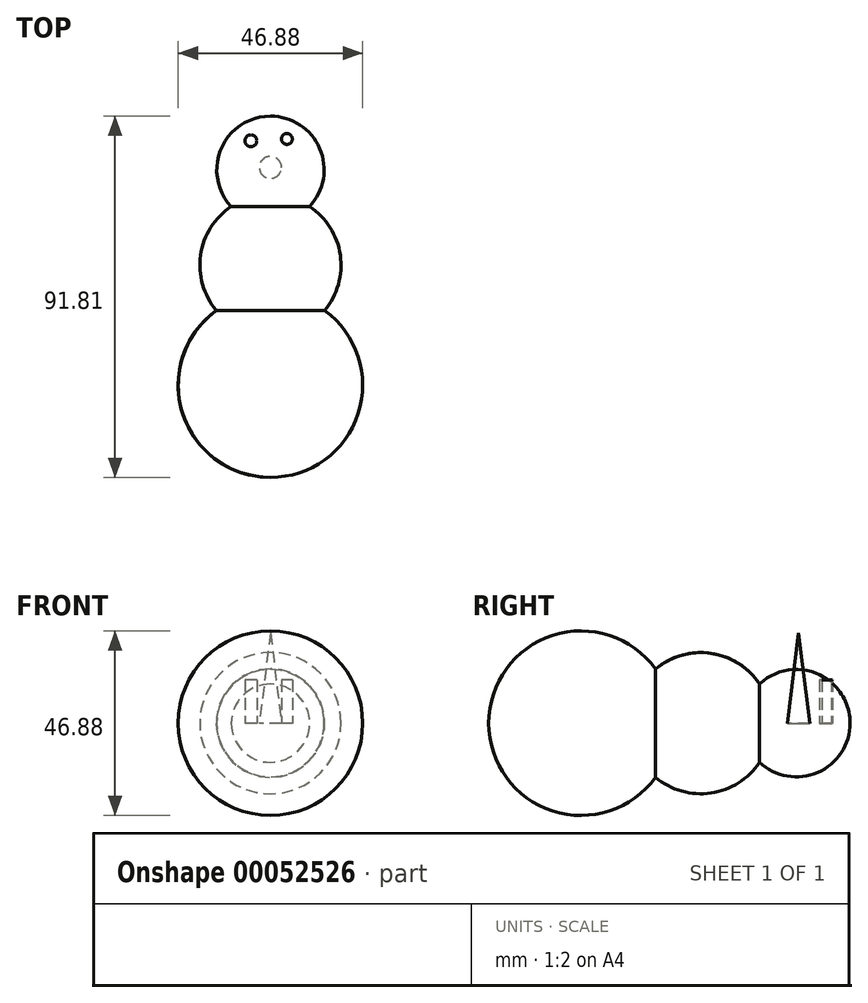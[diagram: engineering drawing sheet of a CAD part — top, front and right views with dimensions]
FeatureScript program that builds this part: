
annotation { "Feature Type Name" : "Feature", "Feature Type Description" : "" }
export const myFeature = defineFeature(function(context is Context, id is Id, definition is map)
    precondition{}
    {
        {
            var Q0;
            Q0=qCreatedBy(makeId("Top.planeOp"),FACE);
            var sketch = newSketch(context, id + "F0", { "sketchPlane" : qUnion([Q0])});
            skArc(sketch, "E0", {"start": v(0, 76.33) * mm, "mid": v(-12.52, 68.12) * mm, "end": v(-9.95, 53.36) * mm});
            skArc(sketch, "E1", {"start": v(-13.76, 26.95) * mm, "mid": v(-22.3, 0.73) * mm, "end": v(0, -15.48) * mm});
            skLineSegment(sketch, "E2", {"start": v(0, 76.33) * mm, "end": v(0, -15.48) * mm});
            skArc(sketch, "E3.trimOffspring", {"start": v(-9.95, 53.36) * mm, "mid": v(-17.75, 41) * mm, "end": v(-13.76, 26.95) * mm});
            skSolve(sketch);
        }
        {
            var Q0;
            Q0=qCreatedBy(makeId("Top.planeOp"),FACE);
            var sketch = newSketch(context, id + "F1", { "sketchPlane" : qUnion([Q0])});
            skCircle(sketch, "E4", {"center": v(0, 63.28) * mm, "radius": 2.82 * mm});
            skSolve(sketch);
        }
        {
            var Q0;
            Q0=makeQuery(id+"F1.imprint","IMPRINT",FACE,{"disambiguationData":[TD([[makeQuery(id+"F1.imprint","IMPRINT",EDGE,{"derivedFrom":sQuery(id+"F1.wireOp",EDGE,"E4")}),1.0]])]});
            extrude(context, id + "F2", {"entities" : qUnion([Q0]), "depth" : 76.2 * mm, "hasDraft" : true, "draftAngle" : 7 * degree, "draftPullDirection" : true});
        }
        {
            var Q0;
            Q0=makeQuery(id+"F0.imprint","IMPRINT",FACE,{"disambiguationData":[TD([[makeQuery(id+"F0.imprint","IMPRINT",EDGE,{"derivedFrom":sQuery(id+"F0.wireOp",EDGE,"E0")}),1.0]])]});
            var Q1;
            Q1=sQuery(id+"F0.wireOp",EDGE,"E2");
            revolve(context, id + "F3", {"entities" : qUnion([Q0]), "axis" : qUnion([Q1]), "revolveType" : RevolveType.FULL});
        }
        {
            var Q0;
            Q0=qCreatedBy(makeId("Top.planeOp"),FACE);
            var sketch = newSketch(context, id + "F4", { "sketchPlane" : qUnion([Q0])});
            skCircle(sketch, "E5", {"center": v(-4.96, 70.07) * mm, "radius": 1.5 * mm});
            skCircle(sketch, "E6", {"center": v(4.17, 70.51) * mm, "radius": 1.4 * mm});
            skSolve(sketch);
        }
        {
            var Q0;
            Q0=makeQuery(id+"F4.imprint","IMPRINT",FACE,{"disambiguationData":[TD([[makeQuery(id+"F4.imprint","IMPRINT",EDGE,{"derivedFrom":sQuery(id+"F4.wireOp",EDGE,"E6")}),1.0]])]});
            var Q1;
            Q1=makeQuery(id+"F4.imprint","IMPRINT",FACE,{"disambiguationData":[TD([[makeQuery(id+"F4.imprint","IMPRINT",EDGE,{"derivedFrom":sQuery(id+"F4.wireOp",EDGE,"E5")}),1.0]])]});
            extrude(context, id + "F5", {"entities" : qUnion([Q0, Q1]), "depth" : 11 * mm});
        }
    });
